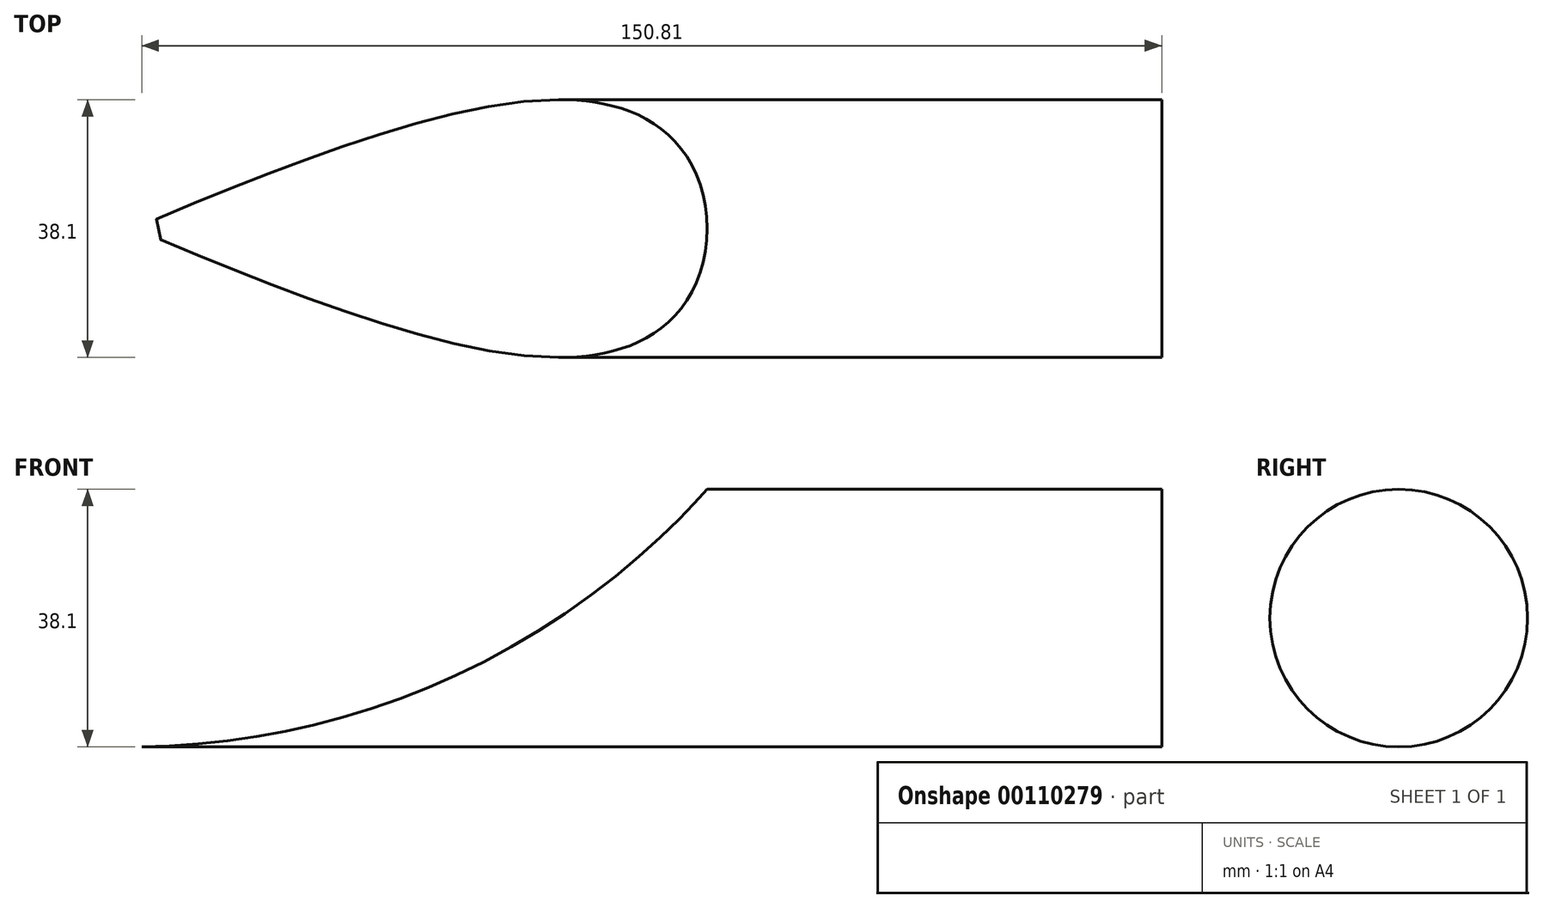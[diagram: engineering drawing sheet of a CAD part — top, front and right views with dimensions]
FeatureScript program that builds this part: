
annotation { "Feature Type Name" : "Feature", "Feature Type Description" : "" }
export const myFeature = defineFeature(function(context is Context, id is Id, definition is map)
    precondition{}
    {
        {
            var Q0;
            Q0=qCreatedBy(makeId("Right.planeOp"),FACE);
            var sketch = newSketch(context, id + "F0", { "sketchPlane" : qUnion([Q0])});
            skCircle(sketch, "E0", {"center": v(0, 0) * mm, "radius": 19.05 * mm});
            skSolve(sketch);
        }
        {
            var Q0;
            Q0=makeQuery(id+"F0.imprint","IMPRINT",FACE,{"disambiguationData":[TD([[makeQuery(id+"F0.imprint","IMPRINT",EDGE,{"derivedFrom":sQuery(id+"F0.wireOp",EDGE,"E0")}),1.0]])]});
            extrude(context, id + "F1", {"entities" : qUnion([Q0]), "depth" : 152.4 * mm});
        }
        {
            var Q0;
            Q0=qCreatedBy(makeId("Front.planeOp"),FACE);
            var sketch = newSketch(context, id + "F2", { "sketchPlane" : qUnion([Q0])});
            skCircle(sketch, "E1", {"center": v(0, 95.24) * mm, "radius": 114.3 * mm});
            skCircle(sketch, "E2", {"center": v(0, 95.24) * mm, "radius": 139.7 * mm});
            skSolve(sketch);
        }
        {
            var Q0;
            Q0=sQuery(id+"F2.wireOp",VERTEX,"E1.center");
            var Q1;
            Q1=makeQuery(id+"F1.opExtrude","SWEPT_BODY",BODY,{"disambiguationData":[OSD([sQuery(id+"F0.wireOp",EDGE,"E0")])]});
            hole(context, id + "F3", {"style" : HoleStyle.SIMPLE, "endStyle" : HoleEndStyle.THROUGH, "holeDiameter" : 228.6 * mm, "startFromSketch" : true, "locations" : qUnion([Q0]), "scope" : qUnion([Q1]), "isTappedThrough" : true});
        }
        {
            var Q0;
            Q0=sQuery(id+"F2.wireOp",VERTEX,"E1.center");
            var Q1;
            Q1=makeQuery(id+"F1.opExtrude","SWEPT_BODY",BODY,{"disambiguationData":[OSD([sQuery(id+"F0.wireOp",EDGE,"E0")])]});
            hole(context, id + "F4", {"style" : HoleStyle.SIMPLE, "endStyle" : HoleEndStyle.THROUGH, "oppositeDirection" : true, "holeDiameter" : 228.6 * mm, "startFromSketch" : true, "locations" : qUnion([Q0]), "scope" : qUnion([Q1]), "isTappedThrough" : true});
        }
    });
